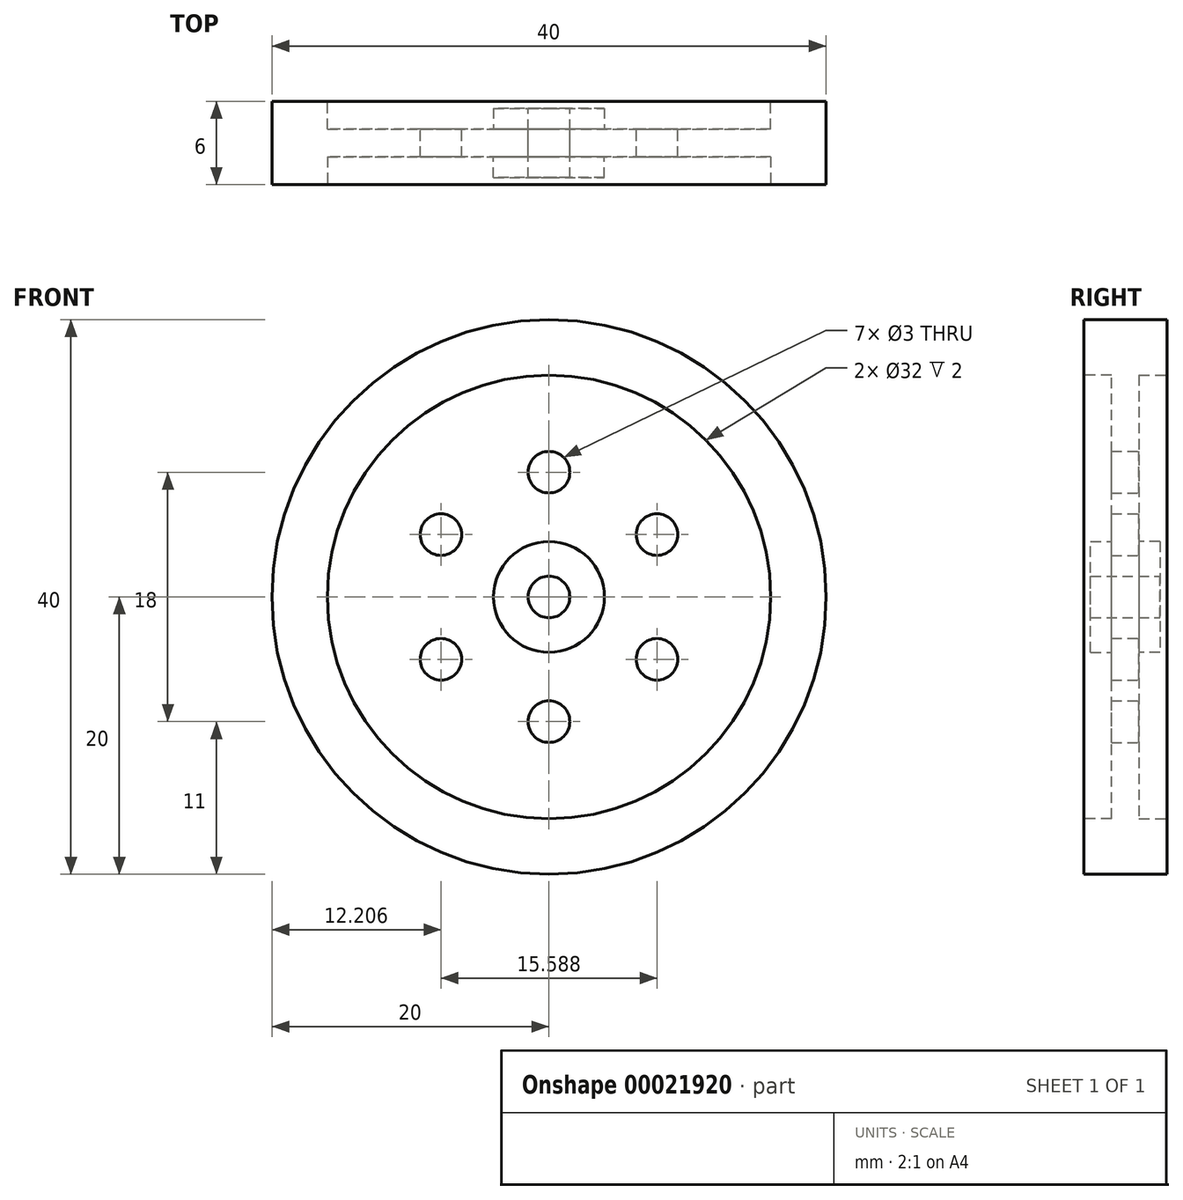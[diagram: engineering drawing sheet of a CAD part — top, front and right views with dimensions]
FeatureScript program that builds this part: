
annotation { "Feature Type Name" : "Feature", "Feature Type Description" : "" }
export const myFeature = defineFeature(function(context is Context, id is Id, definition is map)
    precondition{}
    {
        {
            var Q0;
            Q0=qCreatedBy(makeId("Front.planeOp"),FACE);
            var sketch = newSketch(context, id + "F0", { "sketchPlane" : qUnion([Q0])});
            skCircle(sketch, "E0", {"center": v(0, 0) * mm, "radius": 20 * mm});
            skCircle(sketch, "E1", {"center": v(0, 0) * mm, "radius": 1.5 * mm});
            skLineSegment(sketch, "E2", {"start": v(0, 0) * mm, "end": v(0, 1.5) * mm});
            skCircle(sketch, "E3", {"center": v(0, -9) * mm, "radius": 1.5 * mm});
            skCircle(sketch, "E4", {"center": v(0, 0) * mm, "radius": 17 * mm});
            skCircle(sketch, "E5.1.0", {"center": v(7.8, -4.5) * mm, "radius": 1.5 * mm});
            skCircle(sketch, "E5.2.0", {"center": v(7.8, 4.5) * mm, "radius": 1.5 * mm});
            skCircle(sketch, "E5.3.0", {"center": v(0, 9) * mm, "radius": 1.5 * mm});
            skCircle(sketch, "E5.4.0", {"center": v(-7.8, 4.5) * mm, "radius": 1.5 * mm});
            skCircle(sketch, "E5.5.0", {"center": v(-7.8, -4.5) * mm, "radius": 1.5 * mm});
            skSolve(sketch);
        }
        {
            var Q0;
            Q0=makeQuery(id+"F0.imprint","IMPRINT",FACE,{"disambiguationData":[TD([[makeQuery(id+"F0.imprint","IMPRINT",EDGE,{"derivedFrom":sQuery(id+"F0.wireOp",EDGE,"E0")}),1.0]])]});
            var Q1;
            Q1=makeQuery(id+"F0.imprint","IMPRINT",FACE,{"disambiguationData":[TD([[makeQuery(id+"F0.imprint","IMPRINT",EDGE,{"derivedFrom":sQuery(id+"F0.wireOp",EDGE,"E1")}),-1.0]])]});
            extrude(context, id + "F1", {"entities" : qUnion([Q0, Q1]), "depth" : 6 * mm});
        }
        {
            var Q0;
            Q0=makeQuery(id+"F1.opExtrude","CAP_FACE",FACE,{"disambiguationData":[OSD([sQuery(id+"F0.wireOp",EDGE,"E0"),sQuery(id+"F0.wireOp",EDGE,"E1"),sQuery(id+"F0.wireOp",EDGE,"a8a89c7e-791d-4d1f-b9e0-99226b930afc"),sQuery(id+"F0.wireOp",EDGE,"84881039-aa9d-46e9-b77f-83b9ae0ff2fe"),sQuery(id+"F0.wireOp",EDGE,"73517a91-c14f-49be-a992-abc232131bc5"),sQuery(id+"F0.wireOp",EDGE,"E3"),sQuery(id+"F0.wireOp",EDGE,"e6572f48-1c94-4a00-a566-55d2416ecc9b"),sQuery(id+"F0.wireOp",EDGE,"c8d12710-d7c4-4108-8bbc-ff5f72cee95c")])],"isStart":true});
            var sketch = newSketch(context, id + "F2", { "sketchPlane" : qUnion([Q0])});
            skCircle(sketch, "E6", {"center": v(0, 0) * mm, "radius": 16 * mm});
            skSolve(sketch);
        }
        {
            var Q0;
            Q0=makeQuery(id+"F2.imprint","IMPRINT",FACE,{"disambiguationData":[TD([[makeQuery(id+"F2.imprint","IMPRINT",EDGE,{"derivedFrom":sQuery(id+"F2.wireOp",EDGE,"E6")}),1.0]])]});
            extrude(context, id + "F3", {"entities" : qUnion([Q0]), "operationType" : NewBodyOperationType.REMOVE, "oppositeDirection" : true, "depth" : 2 * mm});
        }
        {
            var Q0;
            Q0=makeQuery(id+"F1.opExtrude","CAP_FACE",FACE,{"disambiguationData":[OSD([sQuery(id+"F0.wireOp",EDGE,"E0"),sQuery(id+"F0.wireOp",EDGE,"E1"),sQuery(id+"F0.wireOp",EDGE,"a8a89c7e-791d-4d1f-b9e0-99226b930afc"),sQuery(id+"F0.wireOp",EDGE,"84881039-aa9d-46e9-b77f-83b9ae0ff2fe"),sQuery(id+"F0.wireOp",EDGE,"73517a91-c14f-49be-a992-abc232131bc5"),sQuery(id+"F0.wireOp",EDGE,"E3"),sQuery(id+"F0.wireOp",EDGE,"e6572f48-1c94-4a00-a566-55d2416ecc9b"),sQuery(id+"F0.wireOp",EDGE,"c8d12710-d7c4-4108-8bbc-ff5f72cee95c")])],"isStart":false});
            var sketch = newSketch(context, id + "F4", { "sketchPlane" : qUnion([Q0])});
            skCircle(sketch, "E7", {"center": v(0, 0) * mm, "radius": 16 * mm});
            skSolve(sketch);
        }
        {
            var Q0;
            Q0=makeQuery(id+"F4.imprint","IMPRINT",FACE,{"disambiguationData":[TD([[makeQuery(id+"F4.imprint","IMPRINT",EDGE,{"derivedFrom":sQuery(id+"F4.wireOp",EDGE,"E7")}),1.0]])]});
            extrude(context, id + "F5", {"entities" : qUnion([Q0]), "operationType" : NewBodyOperationType.REMOVE, "oppositeDirection" : true, "depth" : 2 * mm});
        }
        {
            var Q0;
            Q0=makeQuery(id+"F5.boolean.opBoolean","COPY",FACE,{"derivedFrom":makeQuery(id+"F5.opExtrude","CAP_FACE",FACE,{"disambiguationData":[OSD([sQuery(id+"F0.wireOp",EDGE,"E1"),sQuery(id+"F0.wireOp",EDGE,"a8a89c7e-791d-4d1f-b9e0-99226b930afc"),sQuery(id+"F0.wireOp",EDGE,"84881039-aa9d-46e9-b77f-83b9ae0ff2fe"),sQuery(id+"F0.wireOp",EDGE,"73517a91-c14f-49be-a992-abc232131bc5"),sQuery(id+"F0.wireOp",EDGE,"E3"),sQuery(id+"F0.wireOp",EDGE,"e6572f48-1c94-4a00-a566-55d2416ecc9b"),sQuery(id+"F0.wireOp",EDGE,"c8d12710-d7c4-4108-8bbc-ff5f72cee95c"),sQuery(id+"F4.wireOp",EDGE,"E7")])],"isStart":false})});
            var sketch = newSketch(context, id + "F6", { "sketchPlane" : qUnion([Q0])});
            skCircle(sketch, "E8", {"center": v(0, 0) * mm, "radius": 4 * mm});
            skCircle(sketch, "E9", {"center": v(0, 0) * mm, "radius": 1.5 * mm});
            skSolve(sketch);
        }
        {
            var Q0;
            Q0=makeQuery(id+"F6.imprint","IMPRINT",FACE,{"disambiguationData":[TD([[makeQuery(id+"F6.imprint","IMPRINT",EDGE,{"derivedFrom":sQuery(id+"F6.wireOp",EDGE,"E8")}),1.0]])]});
            extrude(context, id + "F7", {"entities" : qUnion([Q0]), "operationType" : NewBodyOperationType.ADD, "depth" : 1.5 * mm});
        }
        {
            var Q0;
            Q0=makeQuery(id+"F3.boolean.opBoolean","COPY",FACE,{"derivedFrom":makeQuery(id+"F3.opExtrude","CAP_FACE",FACE,{"disambiguationData":[OSD([sQuery(id+"F0.wireOp",EDGE,"E1"),sQuery(id+"F0.wireOp",EDGE,"a8a89c7e-791d-4d1f-b9e0-99226b930afc"),sQuery(id+"F0.wireOp",EDGE,"84881039-aa9d-46e9-b77f-83b9ae0ff2fe"),sQuery(id+"F0.wireOp",EDGE,"73517a91-c14f-49be-a992-abc232131bc5"),sQuery(id+"F0.wireOp",EDGE,"E3"),sQuery(id+"F0.wireOp",EDGE,"e6572f48-1c94-4a00-a566-55d2416ecc9b"),sQuery(id+"F0.wireOp",EDGE,"c8d12710-d7c4-4108-8bbc-ff5f72cee95c"),sQuery(id+"F2.wireOp",EDGE,"E6")])],"isStart":false})});
            var sketch = newSketch(context, id + "F8", { "sketchPlane" : qUnion([Q0])});
            skCircle(sketch, "E10", {"center": v(0, 0) * mm, "radius": 1.5 * mm});
            skCircle(sketch, "E11", {"center": v(0, 0) * mm, "radius": 4 * mm});
            skSolve(sketch);
        }
        {
            var Q0;
            Q0=makeQuery(id+"F8.imprint","IMPRINT",FACE,{"disambiguationData":[TD([[makeQuery(id+"F8.imprint","IMPRINT",EDGE,{"derivedFrom":sQuery(id+"F8.wireOp",EDGE,"E10")}),1.0]])]});
            extrude(context, id + "F9", {"entities" : qUnion([Q0]), "operationType" : NewBodyOperationType.ADD, "depth" : 1.5 * mm});
        }
    });
